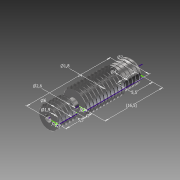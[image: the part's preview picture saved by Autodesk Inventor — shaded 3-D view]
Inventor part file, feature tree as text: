
AUTODESK INVENTOR PART (.ipt)
format: ipt  version: 2015 (Build 190159000, 159)  size: 619,008 bytes
history: native  units: mm
features: other x3, sketch x2, thread x2, revolve x1, extrude x1, chamfer x1
ambient origin geometry x8: Origin, YZ Plane, XZ Plane, XY Plane, X Axis, Y Axis, Z Axis, Center Point
bodies: Body1 (feature_tree)
feature tree (10):
  other  "Твердое тело1"
  sketch  "Эскиз1"
  revolve  "Вращение1"
  thread  "Резьба1"
  other  "Пружина1"
  thread  "Резьба2"
  other  "Пружина2"
  extrude  "Выдавливание1"  Depth=2.0mm
  chamfer  "Фаска1"  Distance=7.0mm
  sketch  "Эскиз2"
